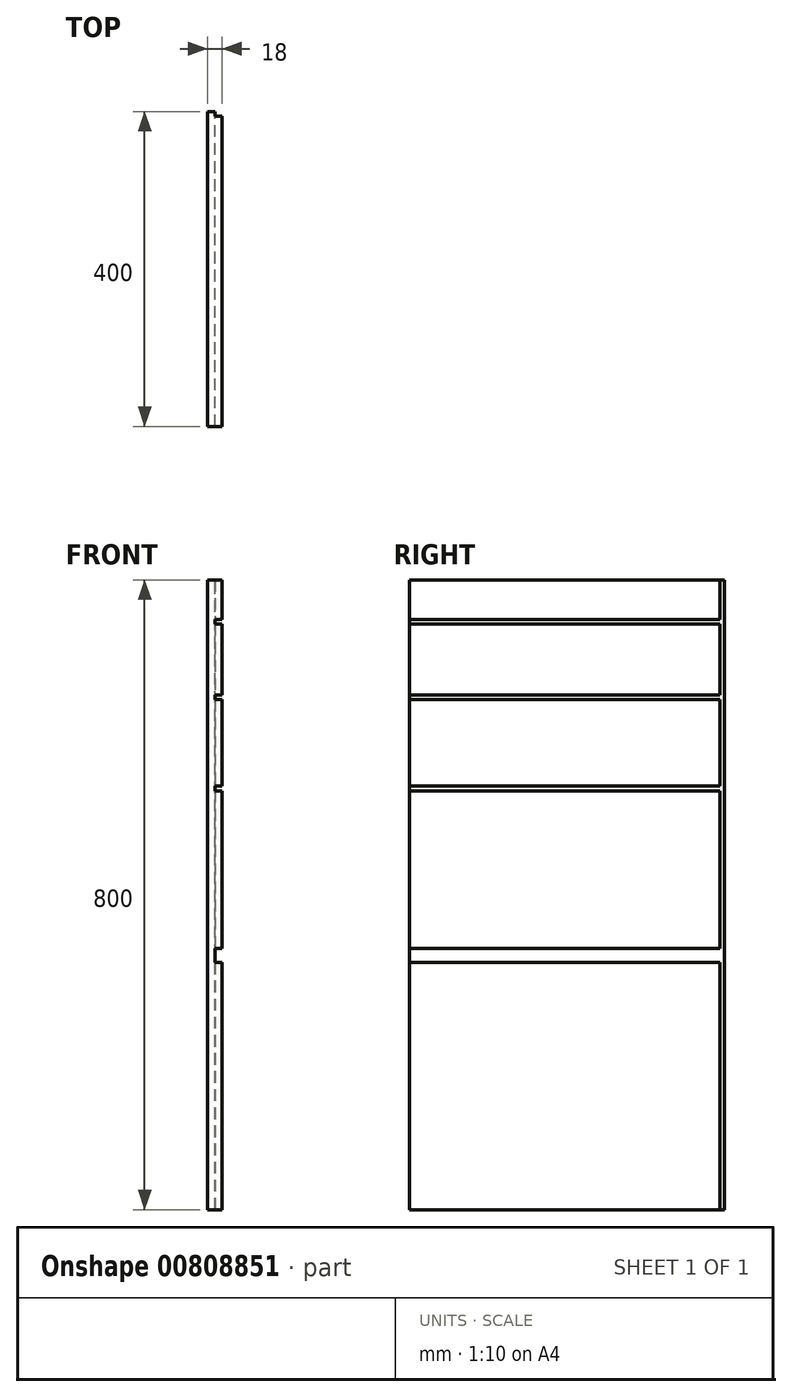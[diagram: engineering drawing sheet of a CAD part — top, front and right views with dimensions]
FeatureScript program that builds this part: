
annotation { "Feature Type Name" : "Feature", "Feature Type Description" : "" }
export const myFeature = defineFeature(function(context is Context, id is Id, definition is map)
    precondition{}
    {
        {
            var Q0;
            Q0=qCreatedBy(makeId("Right.planeOp"),FACE);
            var sketch = newSketch(context, id + "F0", { "sketchPlane" : qUnion([Q0])});
            skLineSegment(sketch, "E0.bottom", {"start": v(0, 0) * mm, "end": v(400, 0) * mm});
            skLineSegment(sketch, "E0.top", {"start": v(0, 800) * mm, "end": v(400, 800) * mm});
            skLineSegment(sketch, "E0.left", {"start": v(0, 0) * mm, "end": v(0, 800) * mm});
            skLineSegment(sketch, "E0.right", {"start": v(400, 0) * mm, "end": v(400, 800) * mm});
            skLineSegment(sketch, "E1.bottom", {"start": v(400, 800) * mm, "end": v(394, 800) * mm});
            skLineSegment(sketch, "E1.top", {"start": v(400, 0) * mm, "end": v(394, 0) * mm});
            skLineSegment(sketch, "E1.left", {"start": v(400, 800) * mm, "end": v(400, 0) * mm});
            skLineSegment(sketch, "E1.right", {"start": v(394, 800) * mm, "end": v(394, 0) * mm});
            skLineSegment(sketch, "E2", {"start": v(0, 800) * mm, "end": v(0, 750) * mm});
            skLineSegment(sketch, "E3.bottom", {"start": v(0, 750) * mm, "end": v(400, 750) * mm});
            skLineSegment(sketch, "E3.top", {"start": v(0, 744) * mm, "end": v(400, 744) * mm});
            skLineSegment(sketch, "E3.left", {"start": v(0, 750) * mm, "end": v(0, 744) * mm});
            skLineSegment(sketch, "E3.right", {"start": v(400, 750) * mm, "end": v(400, 744) * mm});
            skLineSegment(sketch, "E4", {"start": v(0, 744) * mm, "end": v(0, 654) * mm});
            skLineSegment(sketch, "E5.bottom", {"start": v(0, 654) * mm, "end": v(400, 654) * mm});
            skLineSegment(sketch, "E5.top", {"start": v(0, 648) * mm, "end": v(400, 648) * mm});
            skLineSegment(sketch, "E5.left", {"start": v(0, 654) * mm, "end": v(0, 648) * mm});
            skLineSegment(sketch, "E5.right", {"start": v(400, 654) * mm, "end": v(400, 648) * mm});
            skLineSegment(sketch, "E6", {"start": v(0, 648) * mm, "end": v(0, 538) * mm});
            skLineSegment(sketch, "E7.bottom", {"start": v(0, 538) * mm, "end": v(400, 538) * mm});
            skLineSegment(sketch, "E7.top", {"start": v(0, 532) * mm, "end": v(400, 532) * mm});
            skLineSegment(sketch, "E7.left", {"start": v(0, 538) * mm, "end": v(0, 532) * mm});
            skLineSegment(sketch, "E7.right", {"start": v(400, 538) * mm, "end": v(400, 532) * mm});
            skLineSegment(sketch, "E8", {"start": v(0, 532) * mm, "end": v(0, 332) * mm});
            skLineSegment(sketch, "E9.bottom", {"start": v(0, 332) * mm, "end": v(400, 332) * mm});
            skLineSegment(sketch, "E9.top", {"start": v(0, 314) * mm, "end": v(400, 314) * mm});
            skLineSegment(sketch, "E9.left", {"start": v(0, 332) * mm, "end": v(0, 314) * mm});
            skLineSegment(sketch, "E9.right", {"start": v(400, 332) * mm, "end": v(400, 314) * mm});
            skSolve(sketch);
        }
        {
            var Q0;
            {var subQ0=sQuery(id+"F0.wireOp",EDGE,"E0.left");var subQ1=sQuery(id+"F0.wireOp",EDGE,"E0.top");var subQ2=makeQuery(id+"F0.imprint","INTERSECT",VERTEX,{"derivedFrom":[subQ1,subQ0]});Q0=makeQuery(id+"F0.imprint","IMPRINT",FACE,{"disambiguationData":[TD([[makeQuery(id+"F0.imprint","IMPRINT",EDGE,{"disambiguationData":[TD([[subQ2,-1.0]])],"derivedFrom":subQ1}),-1.0]])]});}
            var Q1;
            {var subQ0=sQuery(id+"F0.wireOp",EDGE,"E5.bottom");var subQ1=sQuery(id+"F0.wireOp",EDGE,"E0.left");var subQ2=makeQuery(id+"F0.imprint","INTERSECT",VERTEX,{"derivedFrom":[subQ1,subQ0]});Q1=makeQuery(id+"F0.imprint","IMPRINT",FACE,{"disambiguationData":[TD([[makeQuery(id+"F0.imprint","IMPRINT",EDGE,{"disambiguationData":[TD([[subQ2,-1.0]])],"derivedFrom":subQ1}),-1.0]])]});}
            var Q2;
            {var subQ0=sQuery(id+"F0.wireOp",EDGE,"E5.top");var subQ1=sQuery(id+"F0.wireOp",EDGE,"E0.left");var subQ2=makeQuery(id+"F0.imprint","INTERSECT",VERTEX,{"derivedFrom":[subQ1,subQ0]});Q2=makeQuery(id+"F0.imprint","IMPRINT",FACE,{"disambiguationData":[TD([[makeQuery(id+"F0.imprint","IMPRINT",EDGE,{"disambiguationData":[TD([[subQ2,1.0]])],"derivedFrom":subQ1}),-1.0]])]});}
            var Q3;
            {var subQ0=sQuery(id+"F0.wireOp",EDGE,"E7.top");var subQ1=sQuery(id+"F0.wireOp",EDGE,"E0.left");var subQ2=makeQuery(id+"F0.imprint","INTERSECT",VERTEX,{"derivedFrom":[subQ1,subQ0]});Q3=makeQuery(id+"F0.imprint","IMPRINT",FACE,{"disambiguationData":[TD([[makeQuery(id+"F0.imprint","IMPRINT",EDGE,{"disambiguationData":[TD([[subQ2,1.0]])],"derivedFrom":subQ1}),-1.0]])]});}
            var Q4;
            {var subQ0=sQuery(id+"F0.wireOp",EDGE,"E0.left");var subQ1=sQuery(id+"F0.wireOp",EDGE,"E0.bottom");var subQ2=makeQuery(id+"F0.imprint","INTERSECT",VERTEX,{"derivedFrom":[subQ1,subQ0]});Q4=makeQuery(id+"F0.imprint","IMPRINT",FACE,{"disambiguationData":[TD([[makeQuery(id+"F0.imprint","IMPRINT",EDGE,{"disambiguationData":[TD([[subQ2,-1.0]])],"derivedFrom":subQ1}),1.0]])]});}
            extrude(context, id + "F1", {"entities" : qUnion([Q0, Q1, Q2, Q3, Q4]), "depth" : 18 * mm, "offsetDistance" : 25 * mm});
        }
        {
            var Q0;
            {var subQ0=sQuery(id+"F0.wireOp",EDGE,"E0.right");var subQ1=sQuery(id+"F0.wireOp",EDGE,"E0.top");var subQ2=makeQuery(id+"F0.imprint","INTERSECT",VERTEX,{"derivedFrom":[subQ1,subQ0]});Q0=makeQuery(id+"F0.imprint","IMPRINT",FACE,{"disambiguationData":[TD([[makeQuery(id+"F0.imprint","IMPRINT",EDGE,{"disambiguationData":[TD([[subQ2,1.0]])],"derivedFrom":subQ1}),-1.0]])]});}
            var Q1;
            {var subQ0=sQuery(id+"F0.wireOp",EDGE,"E3.bottom");var subQ1=sQuery(id+"F0.wireOp",EDGE,"E0.right");var subQ2=makeQuery(id+"F0.imprint","INTERSECT",VERTEX,{"derivedFrom":[subQ1,subQ0]});Q1=makeQuery(id+"F0.imprint","IMPRINT",FACE,{"disambiguationData":[TD([[makeQuery(id+"F0.imprint","IMPRINT",EDGE,{"disambiguationData":[TD([[subQ2,1.0]])],"derivedFrom":subQ1}),1.0]])]});}
            var Q2;
            {var subQ0=sQuery(id+"F0.wireOp",EDGE,"E3.top");var subQ1=sQuery(id+"F0.wireOp",EDGE,"E0.right");var subQ2=makeQuery(id+"F0.imprint","INTERSECT",VERTEX,{"derivedFrom":[subQ1,subQ0]});Q2=makeQuery(id+"F0.imprint","IMPRINT",FACE,{"disambiguationData":[TD([[makeQuery(id+"F0.imprint","IMPRINT",EDGE,{"disambiguationData":[TD([[subQ2,1.0]])],"derivedFrom":subQ1}),1.0]])]});}
            var Q3;
            {var subQ0=sQuery(id+"F0.wireOp",EDGE,"E3.bottom");var subQ1=sQuery(id+"F0.wireOp",EDGE,"E0.left");var subQ2=makeQuery(id+"F0.imprint","INTERSECT",VERTEX,{"derivedFrom":[subQ1,subQ0]});Q3=makeQuery(id+"F0.imprint","IMPRINT",FACE,{"disambiguationData":[TD([[makeQuery(id+"F0.imprint","IMPRINT",EDGE,{"disambiguationData":[TD([[subQ2,1.0]])],"derivedFrom":subQ1}),-1.0]])]});}
            var Q4;
            {var subQ0=sQuery(id+"F0.wireOp",EDGE,"E5.bottom");var subQ1=sQuery(id+"F0.wireOp",EDGE,"E0.left");var subQ2=makeQuery(id+"F0.imprint","INTERSECT",VERTEX,{"derivedFrom":[subQ1,subQ0]});Q4=makeQuery(id+"F0.imprint","IMPRINT",FACE,{"disambiguationData":[TD([[makeQuery(id+"F0.imprint","IMPRINT",EDGE,{"disambiguationData":[TD([[subQ2,1.0]])],"derivedFrom":subQ1}),-1.0]])]});}
            var Q5;
            {var subQ0=sQuery(id+"F0.wireOp",EDGE,"E5.bottom");var subQ1=sQuery(id+"F0.wireOp",EDGE,"E0.right");var subQ2=makeQuery(id+"F0.imprint","INTERSECT",VERTEX,{"derivedFrom":[subQ1,subQ0]});Q5=makeQuery(id+"F0.imprint","IMPRINT",FACE,{"disambiguationData":[TD([[makeQuery(id+"F0.imprint","IMPRINT",EDGE,{"disambiguationData":[TD([[subQ2,1.0]])],"derivedFrom":subQ1}),1.0]])]});}
            var Q6;
            {var subQ0=sQuery(id+"F0.wireOp",EDGE,"E5.top");var subQ1=sQuery(id+"F0.wireOp",EDGE,"E0.right");var subQ2=makeQuery(id+"F0.imprint","INTERSECT",VERTEX,{"derivedFrom":[subQ1,subQ0]});Q6=makeQuery(id+"F0.imprint","IMPRINT",FACE,{"disambiguationData":[TD([[makeQuery(id+"F0.imprint","IMPRINT",EDGE,{"disambiguationData":[TD([[subQ2,1.0]])],"derivedFrom":subQ1}),1.0]])]});}
            var Q7;
            {var subQ0=sQuery(id+"F0.wireOp",EDGE,"E7.bottom");var subQ1=sQuery(id+"F0.wireOp",EDGE,"E0.left");var subQ2=makeQuery(id+"F0.imprint","INTERSECT",VERTEX,{"derivedFrom":[subQ1,subQ0]});Q7=makeQuery(id+"F0.imprint","IMPRINT",FACE,{"disambiguationData":[TD([[makeQuery(id+"F0.imprint","IMPRINT",EDGE,{"disambiguationData":[TD([[subQ2,1.0]])],"derivedFrom":subQ1}),-1.0]])]});}
            var Q8;
            {var subQ0=sQuery(id+"F0.wireOp",EDGE,"E7.bottom");var subQ1=sQuery(id+"F0.wireOp",EDGE,"E0.right");var subQ2=makeQuery(id+"F0.imprint","INTERSECT",VERTEX,{"derivedFrom":[subQ1,subQ0]});Q8=makeQuery(id+"F0.imprint","IMPRINT",FACE,{"disambiguationData":[TD([[makeQuery(id+"F0.imprint","IMPRINT",EDGE,{"disambiguationData":[TD([[subQ2,1.0]])],"derivedFrom":subQ1}),1.0]])]});}
            var Q9;
            {var subQ0=sQuery(id+"F0.wireOp",EDGE,"E7.top");var subQ1=sQuery(id+"F0.wireOp",EDGE,"E0.right");var subQ2=makeQuery(id+"F0.imprint","INTERSECT",VERTEX,{"derivedFrom":[subQ1,subQ0]});Q9=makeQuery(id+"F0.imprint","IMPRINT",FACE,{"disambiguationData":[TD([[makeQuery(id+"F0.imprint","IMPRINT",EDGE,{"disambiguationData":[TD([[subQ2,1.0]])],"derivedFrom":subQ1}),1.0]])]});}
            var Q10;
            {var subQ0=sQuery(id+"F0.wireOp",EDGE,"E9.bottom");var subQ1=sQuery(id+"F0.wireOp",EDGE,"E0.left");var subQ2=makeQuery(id+"F0.imprint","INTERSECT",VERTEX,{"derivedFrom":[subQ1,subQ0]});Q10=makeQuery(id+"F0.imprint","IMPRINT",FACE,{"disambiguationData":[TD([[makeQuery(id+"F0.imprint","IMPRINT",EDGE,{"disambiguationData":[TD([[subQ2,1.0]])],"derivedFrom":subQ1}),-1.0]])]});}
            var Q11;
            {var subQ0=sQuery(id+"F0.wireOp",EDGE,"E0.right");var subQ1=sQuery(id+"F0.wireOp",EDGE,"E0.bottom");var subQ2=makeQuery(id+"F0.imprint","INTERSECT",VERTEX,{"derivedFrom":[subQ1,subQ0]});Q11=makeQuery(id+"F0.imprint","IMPRINT",FACE,{"disambiguationData":[TD([[makeQuery(id+"F0.imprint","IMPRINT",EDGE,{"disambiguationData":[TD([[subQ2,1.0]])],"derivedFrom":subQ1}),1.0]])]});}
            var Q12;
            {var subQ0=sQuery(id+"F0.wireOp",EDGE,"E9.bottom");var subQ1=sQuery(id+"F0.wireOp",EDGE,"E0.right");var subQ2=makeQuery(id+"F0.imprint","INTERSECT",VERTEX,{"derivedFrom":[subQ1,subQ0]});Q12=makeQuery(id+"F0.imprint","IMPRINT",FACE,{"disambiguationData":[TD([[makeQuery(id+"F0.imprint","IMPRINT",EDGE,{"disambiguationData":[TD([[subQ2,1.0]])],"derivedFrom":subQ1}),1.0]])]});}
            extrude(context, id + "F2", {"entities" : qUnion([Q0, Q1, Q2, Q3, Q4, Q5, Q6, Q7, Q8, Q9, Q10, Q11, Q12]), "operationType" : NewBodyOperationType.ADD, "depth" : 9 * mm, "offsetDistance" : 25 * mm});
        }
    });
